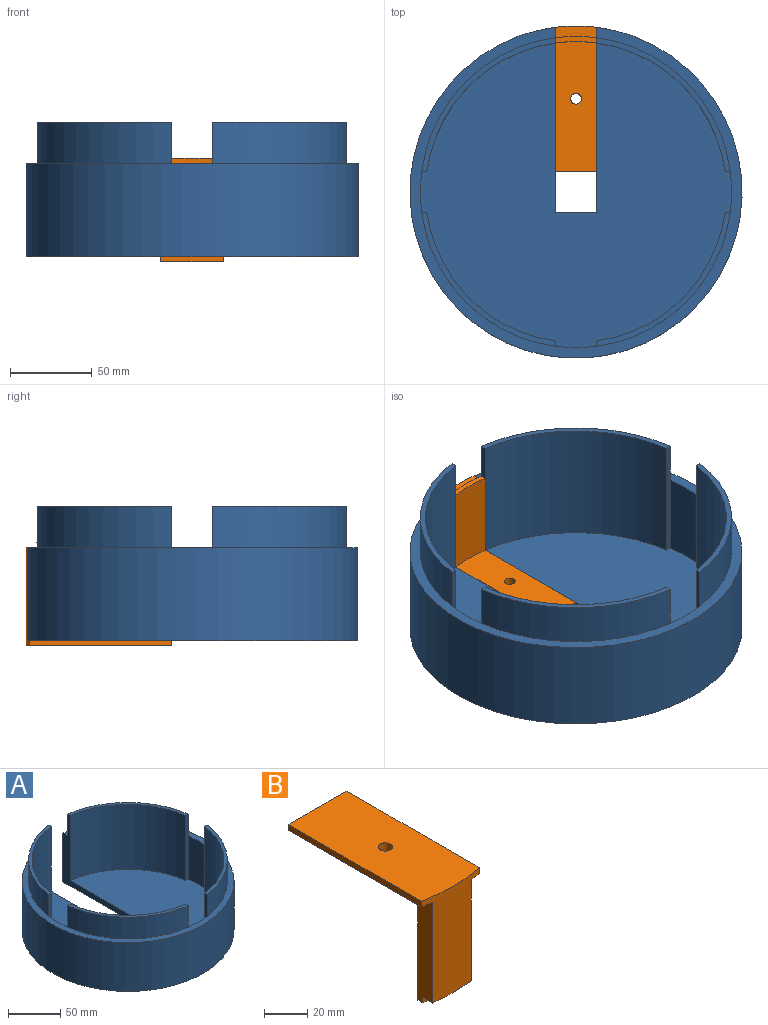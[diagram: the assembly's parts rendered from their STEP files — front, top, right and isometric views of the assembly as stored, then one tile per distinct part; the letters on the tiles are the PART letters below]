
ASSEMBLY  parts=2 mates=1
PART A: 28 faces, bbox 203.2x202.4x82.6 mm
  f0: cylinder r=101.6mm len=203.2mm, axis (0,0,1), area 35027.5mm2, adj f1,f3,f11,f26
  f1: plane 203.2x202.4mm, normal (0,0,-1), area 29532.8mm2, adj f0,f3,f11,f27
  f2: plane 190.5x186.45mm, normal (0,0,1), area 24222.6mm2, adj f3,f5,f6,f8,f9,f11,f13,f15
  f3: plane 113.5x82.55mm, normal (1,0,0), area 1290.2mm2, adj f0,f1,f2,f4,f6,f7,f26,f27
  f4: cylinder r=95.25mm len=81.7mm, axis (0,0,-1), area 3153.2mm2, adj f3,f5,f7,f26
  f5: plane 76.2x3.2mm, normal (0,-1,0), area 244.2mm2, adj f2,f4,f6,f7,f23
  f6: cylinder r=92.08mm len=78.5mm, axis (0,0,-1), area 9079.2mm2, adj f2,f3,f5,f7
  f7: plane 81.7x81.7mm, normal (0,0,1), area 386.2mm2, adj f3,f4,f5,f6
  f8: cylinder r=92.08mm len=78.5mm, axis (0,0,-1), area 9079.2mm2, adj f2,f9,f11,f12
  f9: plane 76.2x3.2mm, normal (0,-1,0), area 244.2mm2, adj f2,f8,f10,f12,f25
  f10: cylinder r=95.25mm len=81.7mm, axis (0,0,-1), area 3153.2mm2, adj f9,f11,f12,f26
  f11: plane 113.5x82.55mm, normal (-1,0,0), area 1290.2mm2, adj f0,f1,f2,f8,f10,f12,f26,f27
  f12: plane 81.7x81.7mm, normal (0,0,1), area 386.2mm2, adj f8,f9,f10,f11
  f13: plane 76.2x3.2mm, normal (-1,0,0), area 244.2mm2, adj f2,f14,f16,f17,f24
  f14: cylinder r=95.25mm len=81.7mm, axis (0,0,-1), area 3153.2mm2, adj f13,f15,f17,f26
  f15: plane 76.2x3.2mm, normal (0,1,0), area 244.2mm2, adj f2,f14,f16,f17,f25
  f16: cylinder r=92.08mm len=78.5mm, axis (0,0,-1), area 9079.2mm2, adj f2,f13,f15,f17
  f17: plane 81.7x81.7mm, normal (0,0,1), area 386.2mm2, adj f13,f14,f15,f16
  f18: cylinder r=92.08mm len=78.5mm, axis (0,0,-1), area 9079.2mm2, adj f2,f19,f21,f22
  f19: plane 76.2x3.2mm, normal (0,1,0), area 244.2mm2, adj f2,f18,f20,f22,f23
  f20: cylinder r=95.25mm len=81.7mm, axis (0,0,-1), area 3153.2mm2, adj f19,f21,f22,f26
  f21: plane 76.2x3.2mm, normal (1,0,0), area 244.2mm2, adj f2,f18,f20,f22,f24
  f22: plane 81.7x81.7mm, normal (0,0,1), area 386.2mm2, adj f18,f19,f20,f21
  f23: cylinder r=95.25mm len=50.8mm, axis (0,0,-1), area 1294.2mm2, adj f2,f5,f19,f26
  f24: cylinder r=95.25mm len=50.8mm, axis (0,0,-1), area 1294.2mm2, adj f2,f13,f21,f26
  f25: extruded ~50.8x25.4mm, area 1294.2mm2, adj f2,f9,f15,f26
  f26: plane 203.2x202.4mm, normal (0,0,1), area 3765.3mm2, adj f0,f3,f4,f10,f11,f14,f20,f23
  f27: plane 25.4x6.35mm, normal (0,1,0), area 161.3mm2, adj f1,f2,f3,f11
PART B: 15 faces, bbox 38.1x88.9x63.5 mm
  f0: plane 88.1x6.35mm, normal (0,0,-1), area 556.5mm2, adj f4,f6,f8,f10
  f1: plane 88.1x6.35mm, normal (0,0,-1), area 556.5mm2, adj f4,f6,f7,f9
  f2: plane 88.9x38.1mm, normal (0,0,1), area 3330mm2, adj f4,f6,f9,f10,f11
  f3: plane 79.38x25.4mm, normal (0,0,-1), area 1974.4mm2, adj f5,f6,f7,f8,f11
  f4: cylinder r=101.6mm len=60.33mm, axis (0,0,-1), area 1577.1mm2, adj f0,f1,f2,f7,f8,f9,f10,f12
  f5: cylinder r=92.08mm len=53.98mm, axis (0,0,1), area 1375.3mm2, adj f3,f7,f8,f14
  f6: plane 38.1x9.53mm, normal (0,1,0), area 282.3mm2, adj f0,f1,f2,f3,f7,f8,f9,f10
  f7: plane 88.1x60.33mm, normal (1,0,0), area 1057.7mm2, adj f1,f3,f4,f5,f6,f12,f13,f14
  f8: plane 88.1x60.33mm, normal (-1,0,0), area 1057.7mm2, adj f0,f3,f4,f5,f6,f12,f13,f14
  f9: plane 87.1x3.18mm, normal (1,0,0), area 276.5mm2, adj f1,f2,f4,f6
  f10: plane 87.1x3.18mm, normal (-1,0,0), area 276.5mm2, adj f0,f2,f4,f6
  f11: cylinder r=3.3mm len=9.53mm, axis (0,0,1), area 197.6mm2, adj f2,f3
  f12: plane 25.4x7.2mm, normal (0,0,-1), area 161.7mm2, adj f4,f7,f8,f13
  f13: cylinder r=95.25mm len=25.4mm, axis (0,0,1), area 80.9mm2, adj f7,f8,f12,f14
  f14: plane 25.4x4.06mm, normal (0,0,-1), area 80.9mm2, adj f5,f7,f8,f13
PLACE A t=(-17.64,7.37,6.76)mm
PLACE B rot(axis=(1,0,0),180deg) t=(-17.64,7.37,6.86)mm
MATE cylindrical A.f0 <-> B.f4  axis (0,0,1) through (-17.64,7.37,28.98)mm
